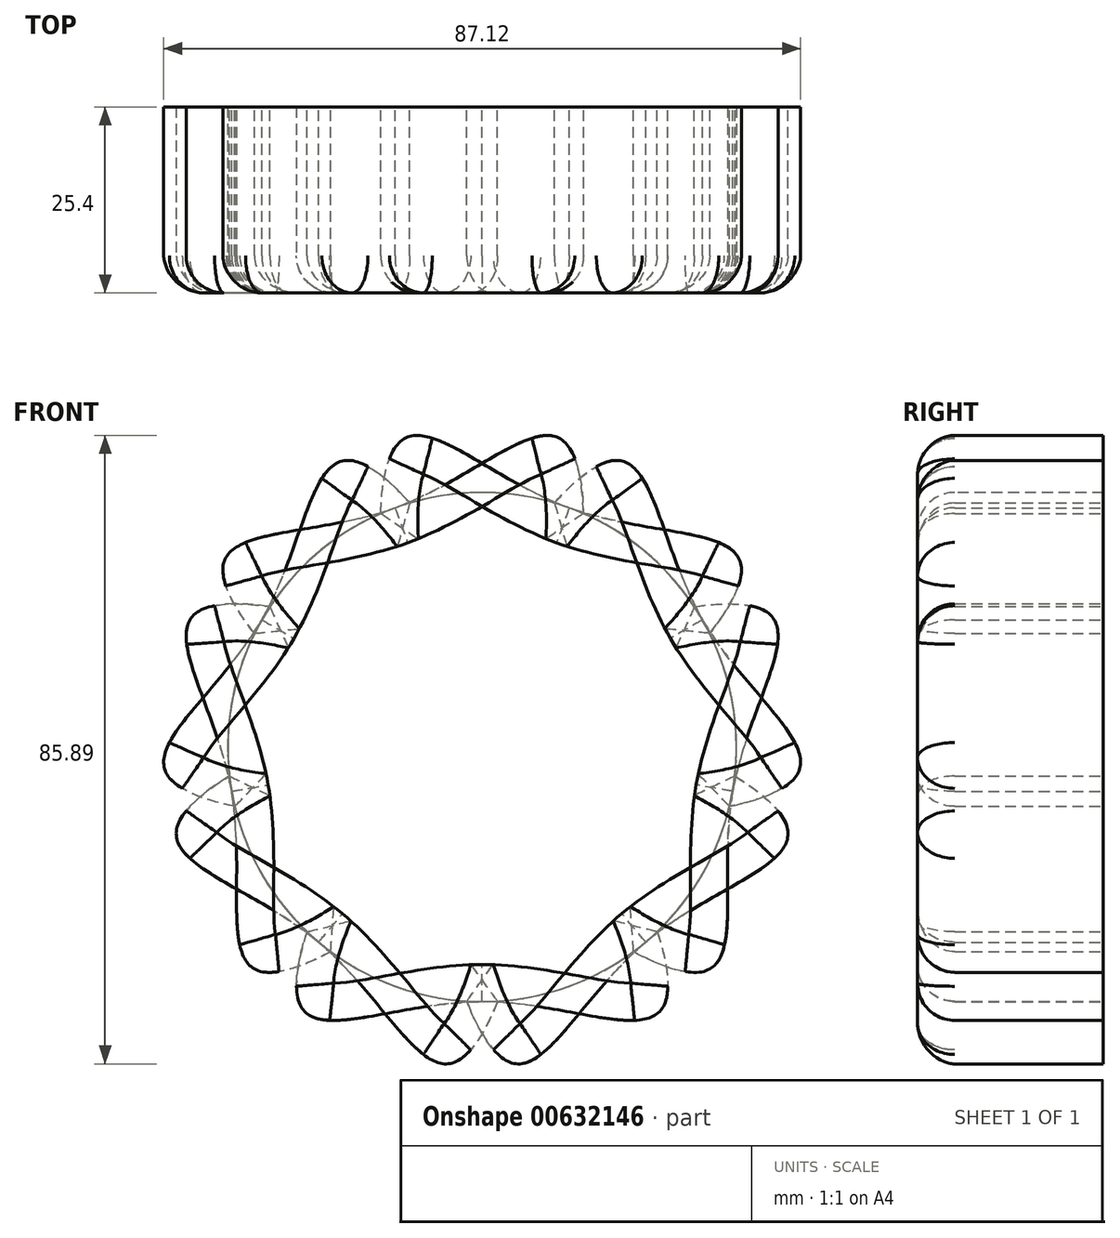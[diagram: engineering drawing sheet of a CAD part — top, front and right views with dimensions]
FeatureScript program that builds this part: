
annotation { "Feature Type Name" : "Feature", "Feature Type Description" : "" }
export const myFeature = defineFeature(function(context is Context, id is Id, definition is map)
    precondition{}
    {
        {
            var Q0;
            Q0=qCreatedBy(makeId("Front.planeOp"),FACE);
            var sketch = newSketch(context, id + "F0", { "sketchPlane" : qUnion([Q0])});
            skFitSpline(sketch, "E0", {"points": [v(0, 0) * mm, v(28.63, 0) * mm, v(0, 34.8) * mm, v(-25.08, 0) * mm, v(0, 0) * mm]});
            skLineSegment(sketch, "E1", {"start": v(0, 34.8) * mm, "end": v(0, 0) * mm});
            skSolve(sketch);
        }
        {
            var Q0;
            {var subQ0=sQuery(id+"F0.wireOp",EDGE,"E1");Q0=makeQuery(id+"F0.imprint","IMPRINT",FACE,{"disambiguationData":[TD([[makeQuery(id+"F0.imprint","IMPRINT",EDGE,{"derivedFrom":subQ0}),-1.0]])]});}
            extrude(context, id + "F1", {"entities" : qUnion([Q0]), "depth" : 25.4 * mm, "offsetDistance" : 25.4 * mm});
        }
        {
            var Q0;
            Q0=makeQuery(id+"F1.opExtrude","SWEPT_FACE",FACE,{"disambiguationData":[OSD([sQuery(id+"F0.wireOp",EDGE,"E1")])]});
            var Q1;
            {var subQ0=sQuery(id+"F0.wireOp",EDGE,"E1");var subQ1=sQuery(id+"F0.wireOp",EDGE,"E0");Q1=makeQuery(id+"F1.opExtrude","SWEPT_EDGE",EDGE,{"disambiguationData":[OSD([subQ1,subQ0]),TDD([makeQuery(id+"F0.imprint","INTERSECT",VERTEX,{"disambiguationData":[OD(0.0)],"derivedFrom":[subQ1,subQ0]})])]});}
            revolve(context, id + "F2", {"operationType" : NewBodyOperationType.ADD, "entities" : qUnion([Q0]), "axis" : qUnion([Q1]), "revolveType" : RevolveType.FULL});
        }
        {
            var Q0;
            Q0=makeQuery(id+"F1.opExtrude","SWEPT_BODY",BODY,{"disambiguationData":[OSD([sQuery(id+"F0.wireOp",EDGE,"E0"),sQuery(id+"F0.wireOp",EDGE,"E1")])]});
            var Q1;
            Q1=qCreatedBy(makeId("Right.planeOp"),FACE);
            mirror(context, id + "F3", {"operationType" : NewBodyOperationType.ADD, "entities" : qUnion([Q0]), "mirrorPlane" : qUnion([Q1])});
        }
        {
            var Q0;
            Q0=makeQuery(id+"F1.opExtrude","SWEPT_BODY",BODY,{"disambiguationData":[OSD([sQuery(id+"F0.wireOp",EDGE,"E0"),sQuery(id+"F0.wireOp",EDGE,"E1")])]});
            var Q1;
            Q1=makeQuery(id+"F2.opRevolve","SWEPT_FACE",FACE,{"disambiguationData":[OSD([sQuery(id+"F0.wireOp",EDGE,"E0"),sQuery(id+"F0.wireOp",EDGE,"E1")])]});
            circularPattern(context, id + "F4", {"entities" : qUnion([Q0]), "axis" : qUnion([Q1]), "angle" : 360 * degree, "instanceCount" : 9, "equalSpace" : true});
        }
        {
            var Q0;
            {var subQ0=sQuery(id+"F0.wireOp",EDGE,"E1");var subQ1=makeQuery(id+"F2.boolean.opBoolean","MERGE",FACE,{"derivedFrom":[makeQuery(id+"F1.opExtrude","CAP_FACE",FACE,{"disambiguationData":[OSD([sQuery(id+"F0.wireOp",EDGE,"E0"),subQ0])],"isStart":false}),makeQuery(id+"F2.opRevolve","SWEPT_FACE",FACE,{"disambiguationData":[OSD([subQ0]),TDD([makeQuery(id+"F1.opExtrude","CAP_EDGE",EDGE,{"disambiguationData":[OSD([subQ0])],"isStart":false})])]})]});Q0=makeQuery(id+"F4.opPattern","COPY",FACE,{"derivedFrom":makeQuery(id+"F3.boolean.opBoolean","MERGE",FACE,{"derivedFrom":[subQ1,makeQuery(id+"F3.opPattern","COPY",FACE,{"derivedFrom":subQ1,"instanceName":"1"})]}),"instanceName":"3"});}
            var Q1;
            {var subQ0=sQuery(id+"F0.wireOp",EDGE,"E1");var subQ1=makeQuery(id+"F2.boolean.opBoolean","MERGE",FACE,{"derivedFrom":[makeQuery(id+"F1.opExtrude","CAP_FACE",FACE,{"disambiguationData":[OSD([sQuery(id+"F0.wireOp",EDGE,"E0"),subQ0])],"isStart":false}),makeQuery(id+"F2.opRevolve","SWEPT_FACE",FACE,{"disambiguationData":[OSD([subQ0]),TDD([makeQuery(id+"F1.opExtrude","CAP_EDGE",EDGE,{"disambiguationData":[OSD([subQ0])],"isStart":false})])]})]});Q1=makeQuery(id+"F4.opPattern","COPY",FACE,{"derivedFrom":makeQuery(id+"F3.boolean.opBoolean","MERGE",FACE,{"derivedFrom":[subQ1,makeQuery(id+"F3.opPattern","COPY",FACE,{"derivedFrom":subQ1,"instanceName":"1"})]}),"instanceName":"1"});}
            var Q2;
            {var subQ0=sQuery(id+"F0.wireOp",EDGE,"E1");var subQ1=makeQuery(id+"F2.boolean.opBoolean","MERGE",FACE,{"derivedFrom":[makeQuery(id+"F1.opExtrude","CAP_FACE",FACE,{"disambiguationData":[OSD([sQuery(id+"F0.wireOp",EDGE,"E0"),subQ0])],"isStart":false}),makeQuery(id+"F2.opRevolve","SWEPT_FACE",FACE,{"disambiguationData":[OSD([subQ0]),TDD([makeQuery(id+"F1.opExtrude","CAP_EDGE",EDGE,{"disambiguationData":[OSD([subQ0])],"isStart":false})])]})]});Q2=makeQuery(id+"F4.opPattern","COPY",FACE,{"derivedFrom":makeQuery(id+"F3.boolean.opBoolean","MERGE",FACE,{"derivedFrom":[subQ1,makeQuery(id+"F3.opPattern","COPY",FACE,{"derivedFrom":subQ1,"instanceName":"1"})]}),"instanceName":"2"});}
            var Q3;
            {var subQ0=sQuery(id+"F0.wireOp",EDGE,"E1");var subQ1=makeQuery(id+"F2.boolean.opBoolean","MERGE",FACE,{"derivedFrom":[makeQuery(id+"F1.opExtrude","CAP_FACE",FACE,{"disambiguationData":[OSD([sQuery(id+"F0.wireOp",EDGE,"E0"),subQ0])],"isStart":false}),makeQuery(id+"F2.opRevolve","SWEPT_FACE",FACE,{"disambiguationData":[OSD([subQ0]),TDD([makeQuery(id+"F1.opExtrude","CAP_EDGE",EDGE,{"disambiguationData":[OSD([subQ0])],"isStart":false})])]})]});Q3=makeQuery(id+"F3.boolean.opBoolean","MERGE",FACE,{"derivedFrom":[subQ1,makeQuery(id+"F3.opPattern","COPY",FACE,{"derivedFrom":subQ1,"instanceName":"1"})]});}
            var Q4;
            {var subQ0=sQuery(id+"F0.wireOp",EDGE,"E1");var subQ1=makeQuery(id+"F2.boolean.opBoolean","MERGE",FACE,{"derivedFrom":[makeQuery(id+"F1.opExtrude","CAP_FACE",FACE,{"disambiguationData":[OSD([sQuery(id+"F0.wireOp",EDGE,"E0"),subQ0])],"isStart":false}),makeQuery(id+"F2.opRevolve","SWEPT_FACE",FACE,{"disambiguationData":[OSD([subQ0]),TDD([makeQuery(id+"F1.opExtrude","CAP_EDGE",EDGE,{"disambiguationData":[OSD([subQ0])],"isStart":false})])]})]});Q4=makeQuery(id+"F4.opPattern","COPY",FACE,{"derivedFrom":makeQuery(id+"F3.boolean.opBoolean","MERGE",FACE,{"derivedFrom":[subQ1,makeQuery(id+"F3.opPattern","COPY",FACE,{"derivedFrom":subQ1,"instanceName":"1"})]}),"instanceName":"8"});}
            var Q5;
            {var subQ0=sQuery(id+"F0.wireOp",EDGE,"E1");var subQ1=makeQuery(id+"F2.boolean.opBoolean","MERGE",FACE,{"derivedFrom":[makeQuery(id+"F1.opExtrude","CAP_FACE",FACE,{"disambiguationData":[OSD([sQuery(id+"F0.wireOp",EDGE,"E0"),subQ0])],"isStart":false}),makeQuery(id+"F2.opRevolve","SWEPT_FACE",FACE,{"disambiguationData":[OSD([subQ0]),TDD([makeQuery(id+"F1.opExtrude","CAP_EDGE",EDGE,{"disambiguationData":[OSD([subQ0])],"isStart":false})])]})]});Q5=makeQuery(id+"F4.opPattern","COPY",FACE,{"derivedFrom":makeQuery(id+"F3.boolean.opBoolean","MERGE",FACE,{"derivedFrom":[subQ1,makeQuery(id+"F3.opPattern","COPY",FACE,{"derivedFrom":subQ1,"instanceName":"1"})]}),"instanceName":"6"});}
            var Q6;
            {var subQ0=sQuery(id+"F0.wireOp",EDGE,"E1");var subQ1=makeQuery(id+"F2.boolean.opBoolean","MERGE",FACE,{"derivedFrom":[makeQuery(id+"F1.opExtrude","CAP_FACE",FACE,{"disambiguationData":[OSD([sQuery(id+"F0.wireOp",EDGE,"E0"),subQ0])],"isStart":false}),makeQuery(id+"F2.opRevolve","SWEPT_FACE",FACE,{"disambiguationData":[OSD([subQ0]),TDD([makeQuery(id+"F1.opExtrude","CAP_EDGE",EDGE,{"disambiguationData":[OSD([subQ0])],"isStart":false})])]})]});Q6=makeQuery(id+"F4.opPattern","COPY",FACE,{"derivedFrom":makeQuery(id+"F3.boolean.opBoolean","MERGE",FACE,{"derivedFrom":[subQ1,makeQuery(id+"F3.opPattern","COPY",FACE,{"derivedFrom":subQ1,"instanceName":"1"})]}),"instanceName":"7"});}
            var Q7;
            {var subQ0=sQuery(id+"F0.wireOp",EDGE,"E1");var subQ1=makeQuery(id+"F2.boolean.opBoolean","MERGE",FACE,{"derivedFrom":[makeQuery(id+"F1.opExtrude","CAP_FACE",FACE,{"disambiguationData":[OSD([sQuery(id+"F0.wireOp",EDGE,"E0"),subQ0])],"isStart":false}),makeQuery(id+"F2.opRevolve","SWEPT_FACE",FACE,{"disambiguationData":[OSD([subQ0]),TDD([makeQuery(id+"F1.opExtrude","CAP_EDGE",EDGE,{"disambiguationData":[OSD([subQ0])],"isStart":false})])]})]});Q7=makeQuery(id+"F4.opPattern","COPY",FACE,{"derivedFrom":makeQuery(id+"F3.boolean.opBoolean","MERGE",FACE,{"derivedFrom":[subQ1,makeQuery(id+"F3.opPattern","COPY",FACE,{"derivedFrom":subQ1,"instanceName":"1"})]}),"instanceName":"5"});}
            var Q8;
            {var subQ0=sQuery(id+"F0.wireOp",EDGE,"E1");var subQ1=makeQuery(id+"F2.boolean.opBoolean","MERGE",FACE,{"derivedFrom":[makeQuery(id+"F1.opExtrude","CAP_FACE",FACE,{"disambiguationData":[OSD([sQuery(id+"F0.wireOp",EDGE,"E0"),subQ0])],"isStart":false}),makeQuery(id+"F2.opRevolve","SWEPT_FACE",FACE,{"disambiguationData":[OSD([subQ0]),TDD([makeQuery(id+"F1.opExtrude","CAP_EDGE",EDGE,{"disambiguationData":[OSD([subQ0])],"isStart":false})])]})]});Q8=makeQuery(id+"F4.opPattern","COPY",FACE,{"derivedFrom":makeQuery(id+"F3.boolean.opBoolean","MERGE",FACE,{"derivedFrom":[subQ1,makeQuery(id+"F3.opPattern","COPY",FACE,{"derivedFrom":subQ1,"instanceName":"1"})]}),"instanceName":"4"});}
            fillet(context, id + "F5", {"entities" : qUnion([Q0, Q1, Q2, Q3, Q4, Q5, Q6, Q7, Q8]), "radius" : 5.08 * mm, "tangentPropagation" : true, "allowEdgeOverflow" : false});
        }
    });
